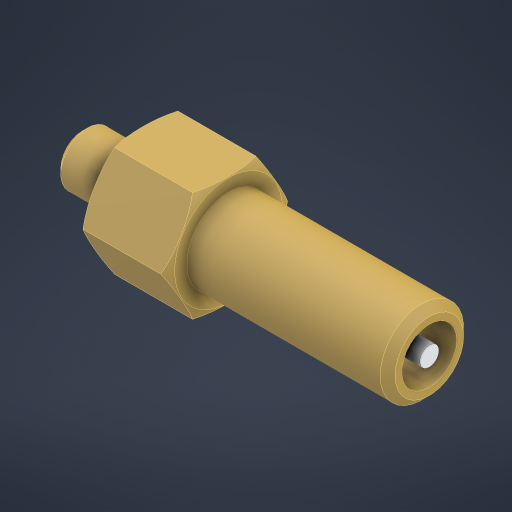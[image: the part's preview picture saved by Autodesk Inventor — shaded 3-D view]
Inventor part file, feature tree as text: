
AUTODESK INVENTOR PART (.ipt)
format: ipt  version: 2024 (Build 280153000, 153)  size: 324,608 bytes
history: native  units: in
note: dims shown in document units (in); Inventor stores cm internally (conversion verified against a paired STEP export)
features: other x2, revolve x1
ambient origin geometry x8: Origin, YZ Plane, XZ Plane, XY Plane, X Axis, Y Axis, Z Axis, Center Point
bodies: Solid1 (feature_tree), Solid2 (feature_tree), Solid3 (feature_tree)
feature tree (3):
  revolve  "Revolve2"  [1 undecoded]
  other  "Boss-Extrude1"
  other  "Cut-Revolve2"
note: 1 required parameter value undecoded (feature->parameter linkage not recoverable at this tier; creation-order binding heuristic only, values carry confidence <= 0.55)
